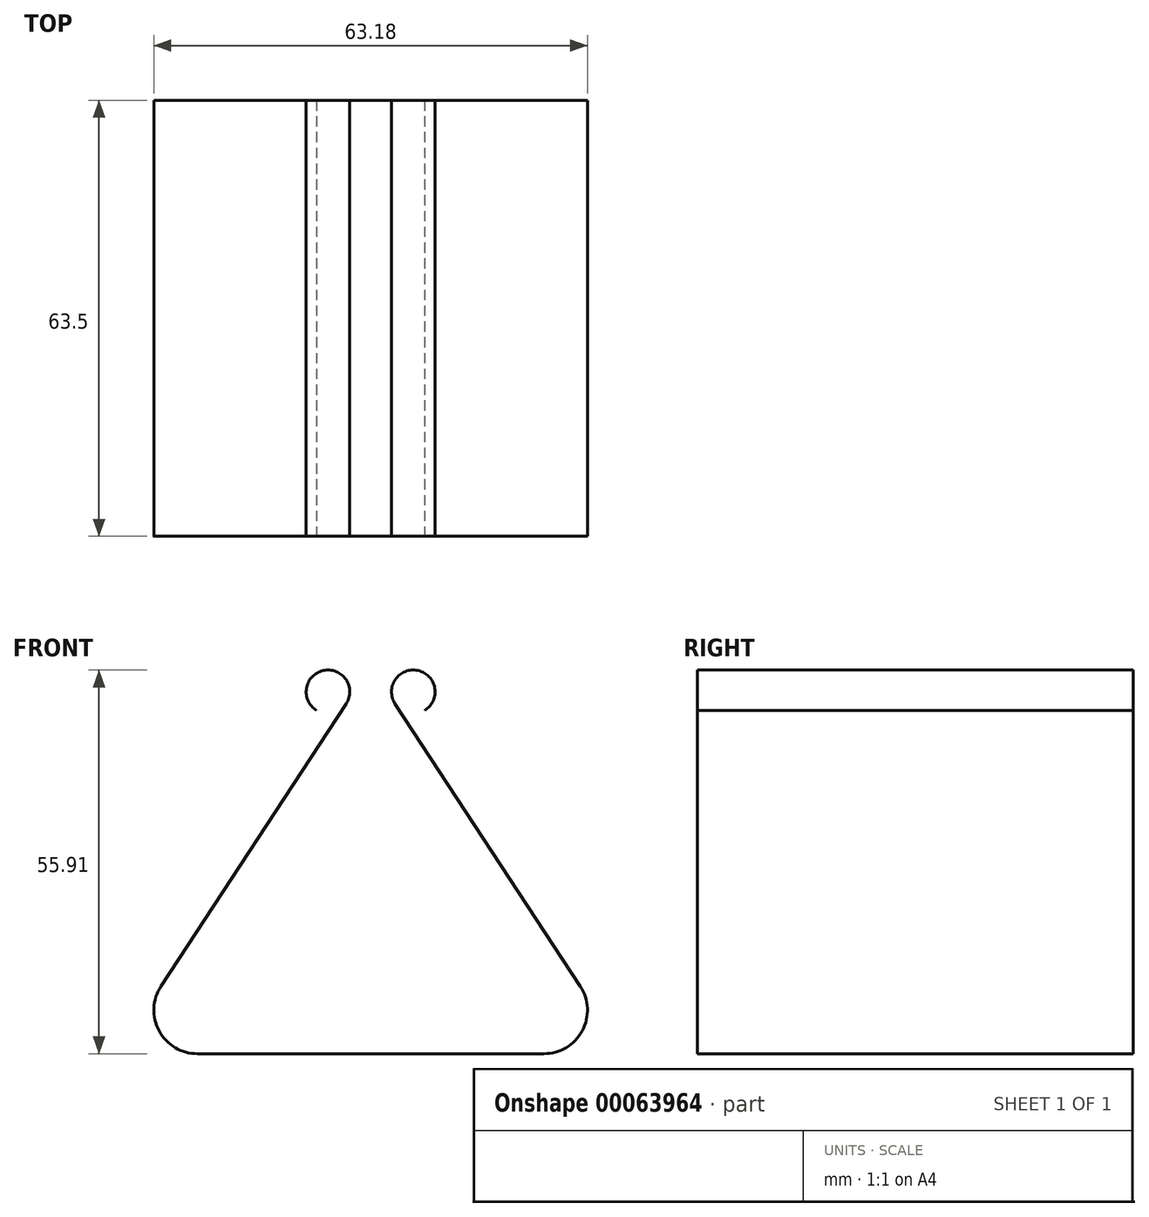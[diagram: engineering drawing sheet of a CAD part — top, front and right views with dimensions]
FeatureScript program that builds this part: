
annotation { "Feature Type Name" : "Feature", "Feature Type Description" : "" }
export const myFeature = defineFeature(function(context is Context, id is Id, definition is map)
    precondition{}
    {
        {
            var Q0;
            Q0=qCreatedBy(makeId("Front.planeOp"),FACE);
            var sketch = newSketch(context, id + "F0", { "sketchPlane" : qUnion([Q0])});
            skLineSegment(sketch, "E0", {"start": v(-3.56, 30.72) * mm, "end": v(-30.55, -10.44) * mm});
            skLineSegment(sketch, "E1", {"start": v(-25.24, -20.27) * mm, "end": v(0, -20.27) * mm});
            skLineSegment(sketch, "E2.MirrorCS", {"start": v(3.56, 30.72) * mm, "end": v(30.55, -10.44) * mm});
            skLineSegment(sketch, "E3.MirrorCS", {"start": v(25.24, -20.27) * mm, "end": v(0, -20.27) * mm});
            skPoint(sketch, "E4.visualSharp", {"position": v(-37, -20.27) * mm});
            skArc(sketch, "E4.filletArc", {"start": v(-30.55, -10.44) * mm, "mid": v(-30.83, -16.94) * mm, "end": v(-25.24, -20.27) * mm});
            skPoint(sketch, "E5.visualSharp", {"position": v(37, -20.27) * mm});
            skArc(sketch, "E5.filletArc", {"start": v(25.24, -20.27) * mm, "mid": v(30.83, -16.94) * mm, "end": v(30.55, -10.44) * mm});
            skArc(sketch, "E6", {"start": v(3.56, 30.72) * mm, "mid": v(6.9, 35.56) * mm, "end": v(7.88, 29.76) * mm});
            skArc(sketch, "E7.MirrorCS", {"start": v(-3.56, 30.72) * mm, "mid": v(-6.9, 35.56) * mm, "end": v(-7.88, 29.76) * mm});
            skSolve(sketch);
        }
        {
            var Q0;
            Q0 = qSketchRegion(id + "F0", true);
            var Q1;
            Q1=sQuery(id+"F0.wireOp",EDGE,"E6");
            var Q2;
            Q2=sQuery(id+"F0.wireOp",EDGE,"E7.MirrorCS");
            var Q3;
            Q3=sQuery(id+"F0.wireOp",EDGE,"E4.filletArc");
            var Q4;
            Q4=sQuery(id+"F0.wireOp",EDGE,"E1");
            var Q5;
            Q5=sQuery(id+"F0.wireOp",EDGE,"E3.MirrorCS");
            var Q6;
            Q6=sQuery(id+"F0.wireOp",EDGE,"E5.filletArc");
            var Q7;
            Q7=sQuery(id+"F0.wireOp",EDGE,"E0");
            var Q8;
            Q8=sQuery(id+"F0.wireOp",EDGE,"E2.MirrorCS");
            extrude(context, id + "F1", {"entities" : qUnion([Q0]), "bodyType" : ToolBodyType.SURFACE, "surfaceEntities" : qUnion([Q1, Q2, Q3, Q4, Q5, Q6, Q7, Q8]), "depth" : 31.75 * mm, "hasDraft" : true, "draftAngle" : 3 * degree, "hasSecondDirection" : true, "secondDirectionOppositeDirection" : true, "secondDirectionDepth" : 31.75 * mm});
        }
        {
            var Q0;
            Q0=qCreatedBy(makeId("Top.planeOp"),FACE);
            cPlane(context, id + "F2", {"entities" : qUnion([Q0]), "cplaneType" : CPlaneType.OFFSET, "offset" : 30.72 * mm, "width" : 152.4 * mm, "height" : 152.4 * mm});
        }
    });
